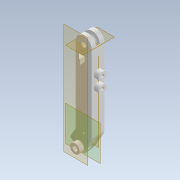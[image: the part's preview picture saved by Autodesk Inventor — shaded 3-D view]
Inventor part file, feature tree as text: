
AUTODESK INVENTOR PART (.ipt)
format: ipt  version: 2020.2 (Build 242310000, 310)  size: 320,512 bytes
history: native  units: mm
features: sketch x12, extrude x11, plane x4, mirror x3, chamfer x2, fillet x2, revolve x1
ambient origin geometry x8: Origin, YZ Plane, XZ Plane, XY Plane, X Axis, Y Axis, Z Axis, Center Point
bodies: Solid1 (feature_tree)
feature tree (35):
  extrude  "base"  Depth=3.0mm
  plane  "Work Plane1"
  plane  "Work Plane2"
  revolve  "Revolution2"  [1 undecoded]
  extrude  "Extrusion8"  Depth=3.5mm
  plane  "Work Plane3"
  extrude  "lock"  Depth=2.5mm
  mirror  "Mirror5"
  chamfer  "Chamfer3"  Distance=40.0mm
  sketch  "Sketch13"  dims[d40=4.0mm d41=3.0mm]
  fillet  "Fillet5"  Radius=6.0mm
  extrude  "motor_1"  Depth=5.0mm
  extrude  "tensor_1"  Depth=3.0mm TaperAngle=45.0deg
  extrude  "tensor_2"  Depth=3.0mm
  extrude  "Extrusion14"  Depth=3.0mm
  extrude  "Extrusion15"  Depth=2.5mm
  plane  "Work Plane4"
  extrude  "Extrusion16"  Depth=5.0mm TaperAngle=0.0deg
  extrude  "lock_1"  Depth=3.0mm
  mirror  "Mirror2"
  chamfer  "Chamfer2"  Distance=3.0mm
  extrude  "lock_2"  Depth=3.0mm TaperAngle=45.0deg
  mirror  "Mirror3"
  fillet  "Fillet3"  Radius=10.0mm
  sketch  "Sketch1"  dims[d1=48.0mm d2=3.0mm]
  sketch  "Sketch4"  dims[d3=10.0mm d4=10.0mm]
  sketch  "Sketch7"  dims[d5=8.0mm d6=0.0mm d20=3.5mm]
  sketch  "Sketch9"  dims[d21=3.5mm d23=2.5mm d24=40.0mm d25=0.0mm d32=6.0mm]
  sketch  "Sketch10"  dims[d33=13.962634mm d34=5.0mm]
  sketch  "Sketch12"  dims[d35=3.0mm d36=0.0mm d37=3.0mm d38=2.0mm d39=45.0deg]
  sketch  "Sketch14"  dims[d42=3.0mm d43=0.0mm d44=3.0mm]
  sketch  "Sketch15"  dims[d47=3.5mm d48=2.5mm]
  sketch  "Sketch16"  dims[d49=180.0deg d50=5.0mm d51=0.0mm]
  sketch  "Sketch17"  dims[d57=6.0mm d58=3.0mm]
  sketch  "Sketch19"  dims[d59=14.835299mm d60=3.0mm d61=0.0mm d62=3.0mm d63=2.0mm d64=45.0deg d65=10.0mm d66=120.0deg d68=4.0mm d69=3.0mm d70=40.899mm d71=0.0mm d72=15.0mm d73=7.0mm d74=5.0mm d75=5.0mm d76=3.0mm d77=0.0mm d78=2.0mm d79=2.0mm d80=10.0mm d81=0.0mm d82=5.0mm d83=10.0mm d84=0.0mm d85=3.0mm d86=10.0mm d87=0.0mm d88=3.0mm d89=6.0mm d90=10.0mm d91=0.0mm d92=3.0mm]
note: 1 required parameter value undecoded (feature->parameter linkage not recoverable at this tier; creation-order binding heuristic only, values carry confidence <= 0.55)
